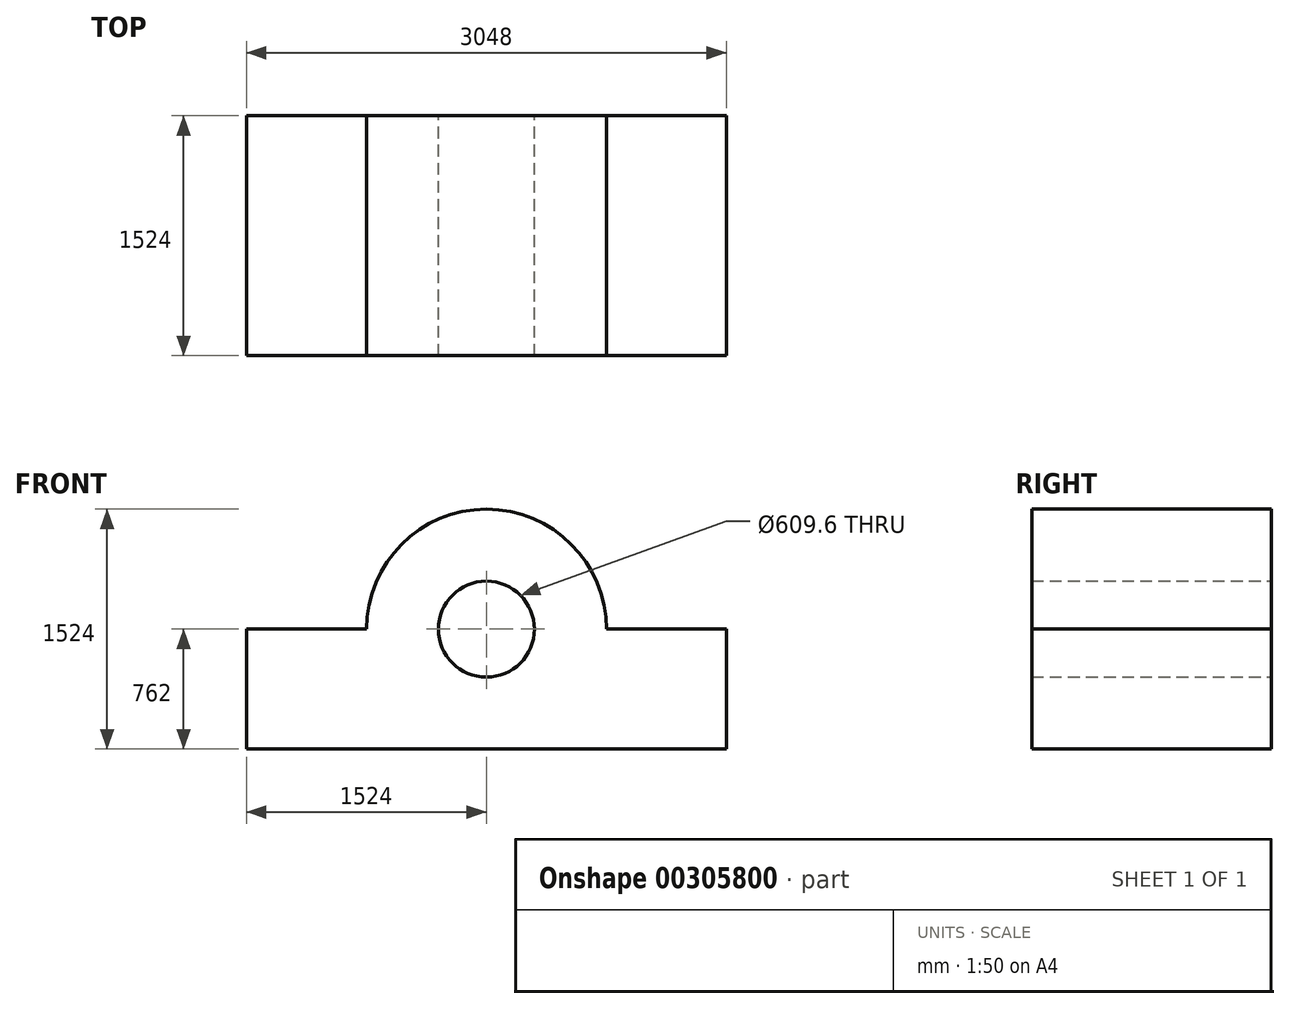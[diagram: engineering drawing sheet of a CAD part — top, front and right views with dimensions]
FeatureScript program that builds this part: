
annotation { "Feature Type Name" : "Feature", "Feature Type Description" : "" }
export const myFeature = defineFeature(function(context is Context, id is Id, definition is map)
    precondition{}
    {
        {
            var Q0;
            Q0=qCreatedBy(makeId("Front.planeOp"),FACE);
            var sketch = newSketch(context, id + "F0", { "sketchPlane" : qUnion([Q0])});
            skCircle(sketch, "E0", {"center": v(0, 0) * mm, "radius": 304.8 * mm});
            skCircle(sketch, "E1", {"center": v(0, 0) * mm, "radius": 762 * mm});
            skLineSegment(sketch, "E2", {"start": v(-762, 0) * mm, "end": v(-1524, 0) * mm});
            skLineSegment(sketch, "E3", {"start": v(-1524, 0) * mm, "end": v(-1524, -762) * mm});
            skLineSegment(sketch, "E4", {"start": v(-1524, -762) * mm, "end": v(1524, -762) * mm});
            skLineSegment(sketch, "E5", {"start": v(1524, -762) * mm, "end": v(1524, 0) * mm});
            skLineSegment(sketch, "E6", {"start": v(1524, 0) * mm, "end": v(762, 0) * mm});
            skSolve(sketch);
        }
        {
            var Q0;
            Q0 = qSketchRegion(id + "F0", true);
            extrude(context, id + "F1", {"entities" : qUnion([Q0]), "depth" : 1524 * mm});
        }
    });
